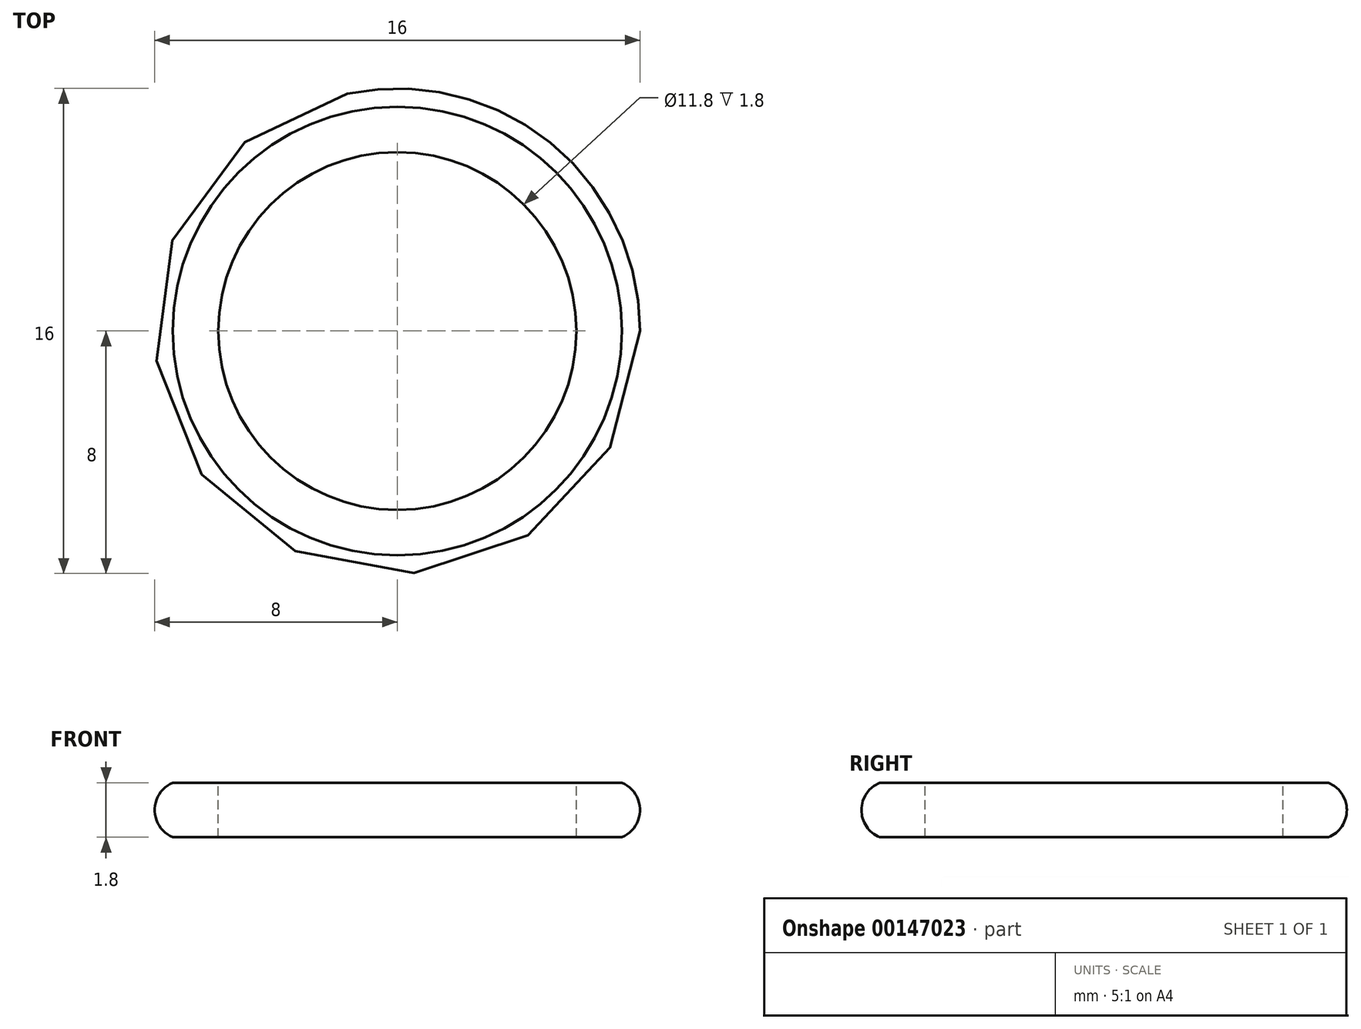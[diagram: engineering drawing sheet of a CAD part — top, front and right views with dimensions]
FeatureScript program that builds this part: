
annotation { "Feature Type Name" : "Feature", "Feature Type Description" : "" }
export const myFeature = defineFeature(function(context is Context, id is Id, definition is map)
    precondition{}
    {
        {
            var Q0;
            Q0=qCreatedBy(makeId("Front.planeOp"),FACE);
            var sketch = newSketch(context, id + "F0", { "sketchPlane" : qUnion([Q0])});
            skArc(sketch, "E0", {"start": v(0, 1.8) * mm, "mid": v(-0.6, 0.9) * mm, "end": v(0, 0) * mm});
            skLineSegment(sketch, "E1", {"start": v(0, 1.8) * mm, "end": v(1.5, 1.8) * mm});
            skLineSegment(sketch, "E2", {"start": v(1.5, 1.8) * mm, "end": v(1.5, 0) * mm});
            skLineSegment(sketch, "E3", {"start": v(1.5, 0) * mm, "end": v(0, 0) * mm});
            skLineSegment(sketch, "E4", {"start": v(7.4, 3.18) * mm, "end": v(7.4, -2.55) * mm});
            skSolve(sketch);
        }
        {
            var Q0;
            Q0=makeQuery(id+"F0.imprint","IMPRINT",FACE,{"disambiguationData":[TD([[makeQuery(id+"F0.imprint","IMPRINT",EDGE,{"derivedFrom":sQuery(id+"F0.wireOp",EDGE,"E0")}),1.0]])]});
            var Q1;
            Q1=sQuery(id+"F0.wireOp",EDGE,"E4");
            revolve(context, id + "F1", {"entities" : qUnion([Q0]), "axis" : qUnion([Q1]), "revolveType" : RevolveType.FULL});
        }
    });
